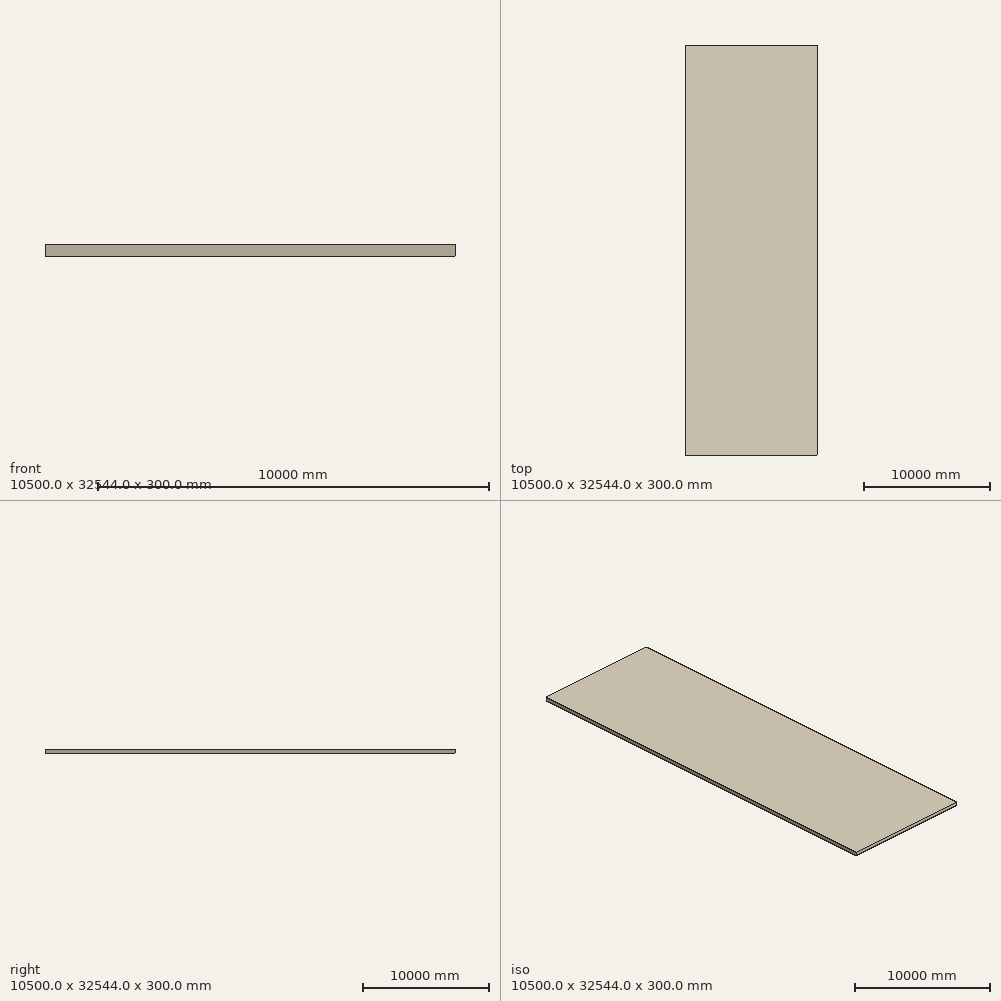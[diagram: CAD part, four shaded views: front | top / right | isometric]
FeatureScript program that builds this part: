
annotation { "Feature Type Name" : "Feature", "Feature Type Description" : "" }
export const myFeature = defineFeature(function(context is Context, id is Id, definition is map)
    precondition{}
    {
        {
            var Q0;
            Q0=qCreatedBy(makeId("Top.planeOp"),FACE);
            var sketch = newSketch(context, id + "F0", { "sketchPlane" : qUnion([Q0])});
            skLineSegment(sketch, "E0.bottom", {"start": v(0, 0) * mm, "end": v(10500, 0) * mm});
            skLineSegment(sketch, "E0.top", {"start": v(0, -32544) * mm, "end": v(10500, -32544) * mm});
            skLineSegment(sketch, "E0.left", {"start": v(0, 0) * mm, "end": v(0, -32544) * mm});
            skLineSegment(sketch, "E0.right", {"start": v(10500, 0) * mm, "end": v(10500, -32544) * mm});
            skSolve(sketch);
        }
        {
            var Q0;
            Q0 = qSketchRegion(id + "F0", true);
            extrude(context, id + "F1", {"entities" : qUnion([Q0]), "depth" : 300 * mm});
        }
    });
